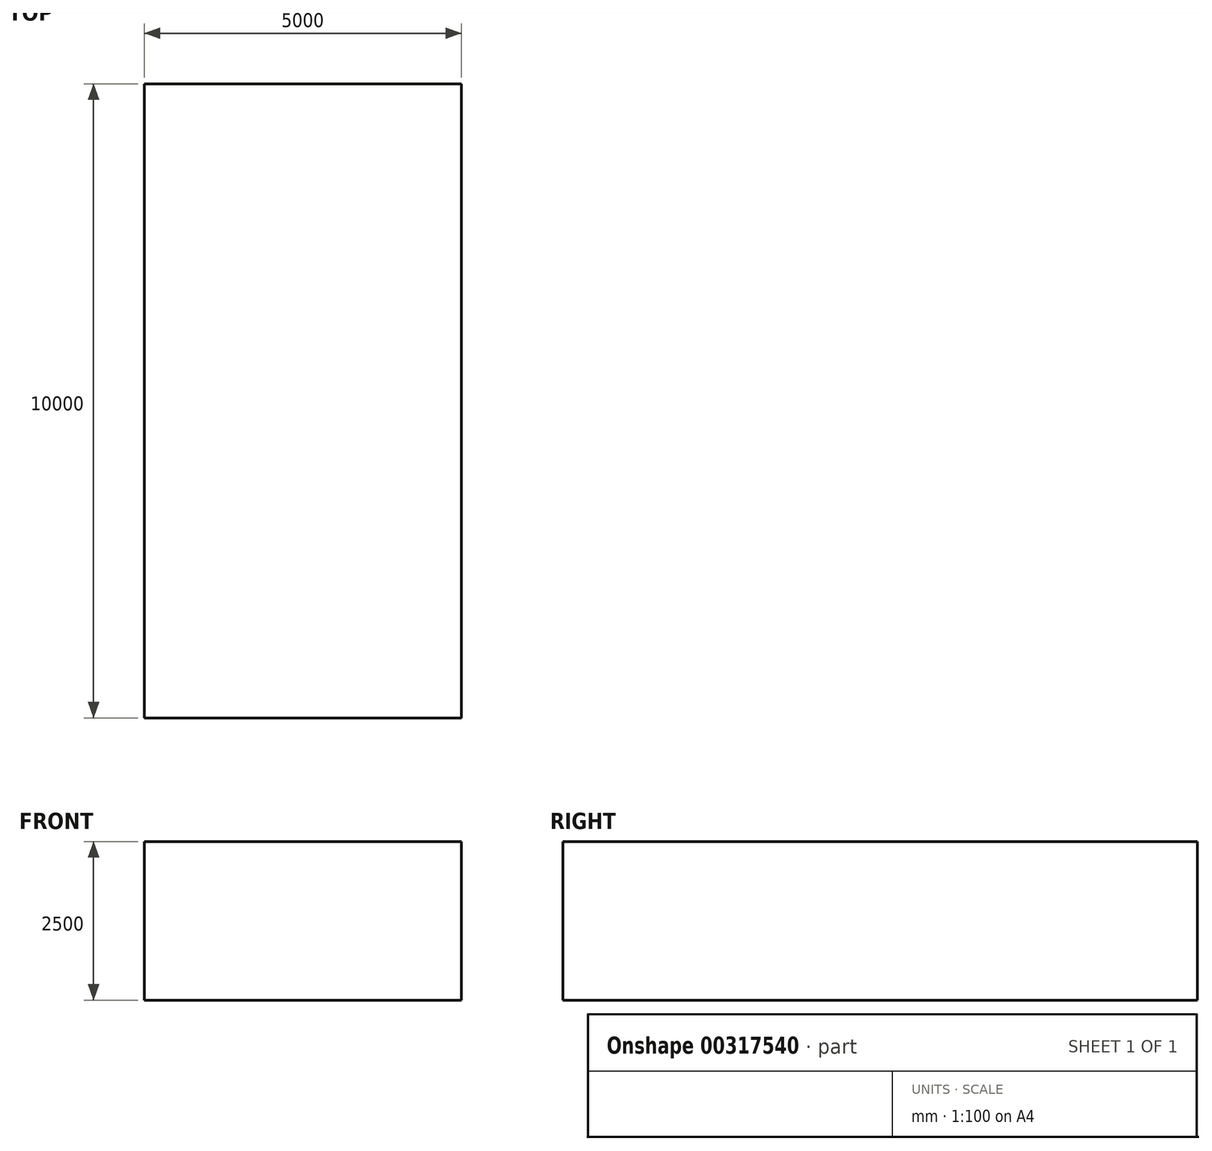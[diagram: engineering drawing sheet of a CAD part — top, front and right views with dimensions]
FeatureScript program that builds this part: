
annotation { "Feature Type Name" : "Feature", "Feature Type Description" : "" }
export const myFeature = defineFeature(function(context is Context, id is Id, definition is map)
    precondition{}
    {
        {
            var Q0;
            Q0=qCreatedBy(makeId("Front.planeOp"),FACE);
            var sketch = newSketch(context, id + "F0", { "sketchPlane" : qUnion([Q0])});
            skLineSegment(sketch, "E0.bottom", {"start": v(0, 0) * mm, "end": v(5000, 0) * mm});
            skLineSegment(sketch, "E0.top", {"start": v(0, -2500) * mm, "end": v(5000, -2500) * mm});
            skLineSegment(sketch, "E0.left", {"start": v(0, 0) * mm, "end": v(0, -2500) * mm});
            skLineSegment(sketch, "E0.right", {"start": v(5000, 0) * mm, "end": v(5000, -2500) * mm});
            skSolve(sketch);
        }
        {
            var Q0;
            Q0 = qSketchRegion(id + "F0", true);
            extrude(context, id + "F1", {"entities" : qUnion([Q0]), "depth" : 10000 * mm});
        }
    });
